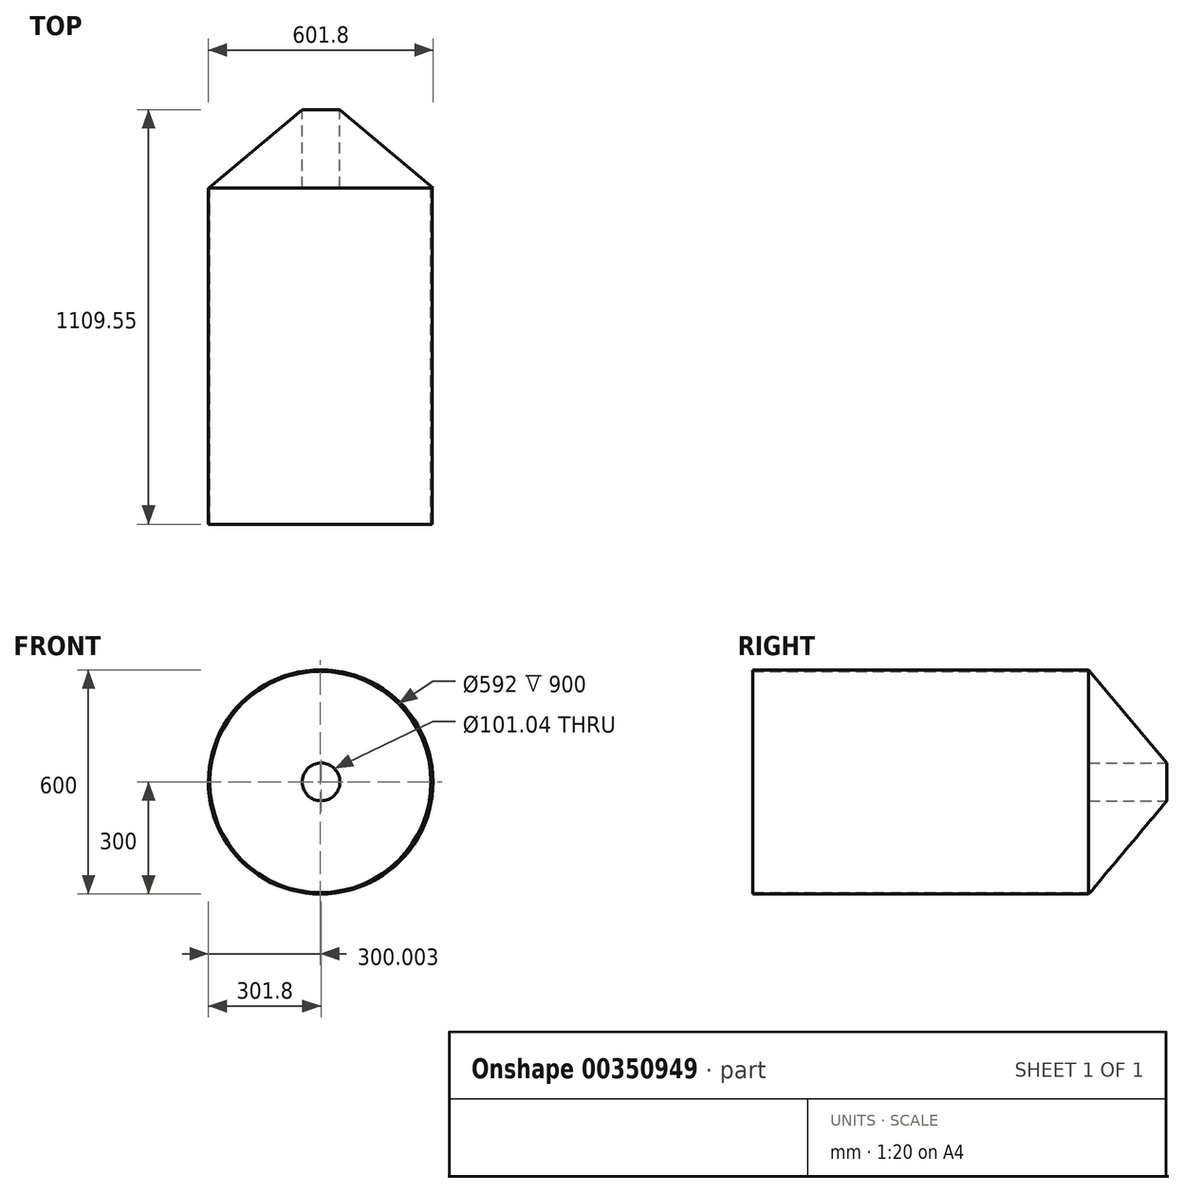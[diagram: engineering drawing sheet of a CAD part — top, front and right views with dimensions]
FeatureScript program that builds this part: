
annotation { "Feature Type Name" : "Feature", "Feature Type Description" : "" }
export const myFeature = defineFeature(function(context is Context, id is Id, definition is map)
    precondition{}
    {
        {
            var Q0;
            Q0=qCreatedBy(makeId("Front.planeOp"),FACE);
            var sketch = newSketch(context, id + "F0", { "sketchPlane" : qUnion([Q0])});
            skCircle(sketch, "E0", {"center": v(-1.8, 0) * mm, "radius": 300 * mm});
            skCircle(sketch, "E1", {"center": v(-1.8, 0) * mm, "radius": 296 * mm});
            skSolve(sketch);
        }
        {
            var Q0;
            Q0 = qSketchRegion(id + "F0", true);
            extrude(context, id + "F1", {"entities" : qUnion([Q0]), "depth" : 900 * mm});
        }
        {
            var Q0;
            Q0=qCreatedBy(makeId("Right.planeOp"),FACE);
            var sketch = newSketch(context, id + "F2", { "sketchPlane" : qUnion([Q0])});
            skLineSegment(sketch, "E2", {"start": v(0, 0) * mm, "end": v(0, 300) * mm});
            skLineSegment(sketch, "E3", {"start": v(0, 0) * mm, "end": v(0, -300) * mm});
            skLineSegment(sketch, "E4", {"start": v(0, -300) * mm, "end": v(209.55, -50.52) * mm});
            skLineSegment(sketch, "E5", {"start": v(0, 0) * mm, "end": v(209.55, 0) * mm});
            skLineSegment(sketch, "E6", {"start": v(209.55, 0) * mm, "end": v(209.55, -50.52) * mm});
            skSolve(sketch);
        }
        {
            var Q0;
            Q0=makeQuery(id+"F2.imprint","IMPRINT",FACE,{"disambiguationData":[TD([[makeQuery(id+"F2.imprint","IMPRINT",EDGE,{"derivedFrom":sQuery(id+"F2.wireOp",EDGE,"E3")}),1.0]])]});
            var Q1;
            Q1=sQuery(id+"F2.wireOp",EDGE,"E5");
            revolve(context, id + "F3", {"operationType" : NewBodyOperationType.ADD, "entities" : qUnion([Q0]), "axis" : qUnion([Q1]), "revolveType" : RevolveType.FULL});
        }
        {
            var Q0;
            Q0=makeQuery(id+"F3.opRevolve","SWEPT_FACE",FACE,{"disambiguationData":[OSD([sQuery(id+"F2.wireOp",EDGE,"E6")])]});
            var sketch = newSketch(context, id + "F4", { "sketchPlane" : qUnion([Q0])});
            skSolve(sketch);
        }
        {
            var Q0;
            Q0 = qSketchRegion(id + "F4", true);
            var Q1;
            Q1=makeQuery(id+"F4.imprint","IMPRINT",FACE,{"disambiguationData":[TD([[makeQuery(id+"F4.imprint","IMPRINT",EDGE,{"derivedFrom":makeQuery(id+"F3.opRevolve","SWEPT_EDGE",EDGE,{"disambiguationData":[OSD([sQuery(id+"F2.wireOp",EDGE,"E4"),sQuery(id+"F2.wireOp",EDGE,"E6")])]})}),-1.0]])]});
            extrude(context, id + "F5", {"entities" : qUnion([Q0, Q1]), "operationType" : NewBodyOperationType.REMOVE, "oppositeDirection" : true, "depth" : 250 * mm});
        }
    });
